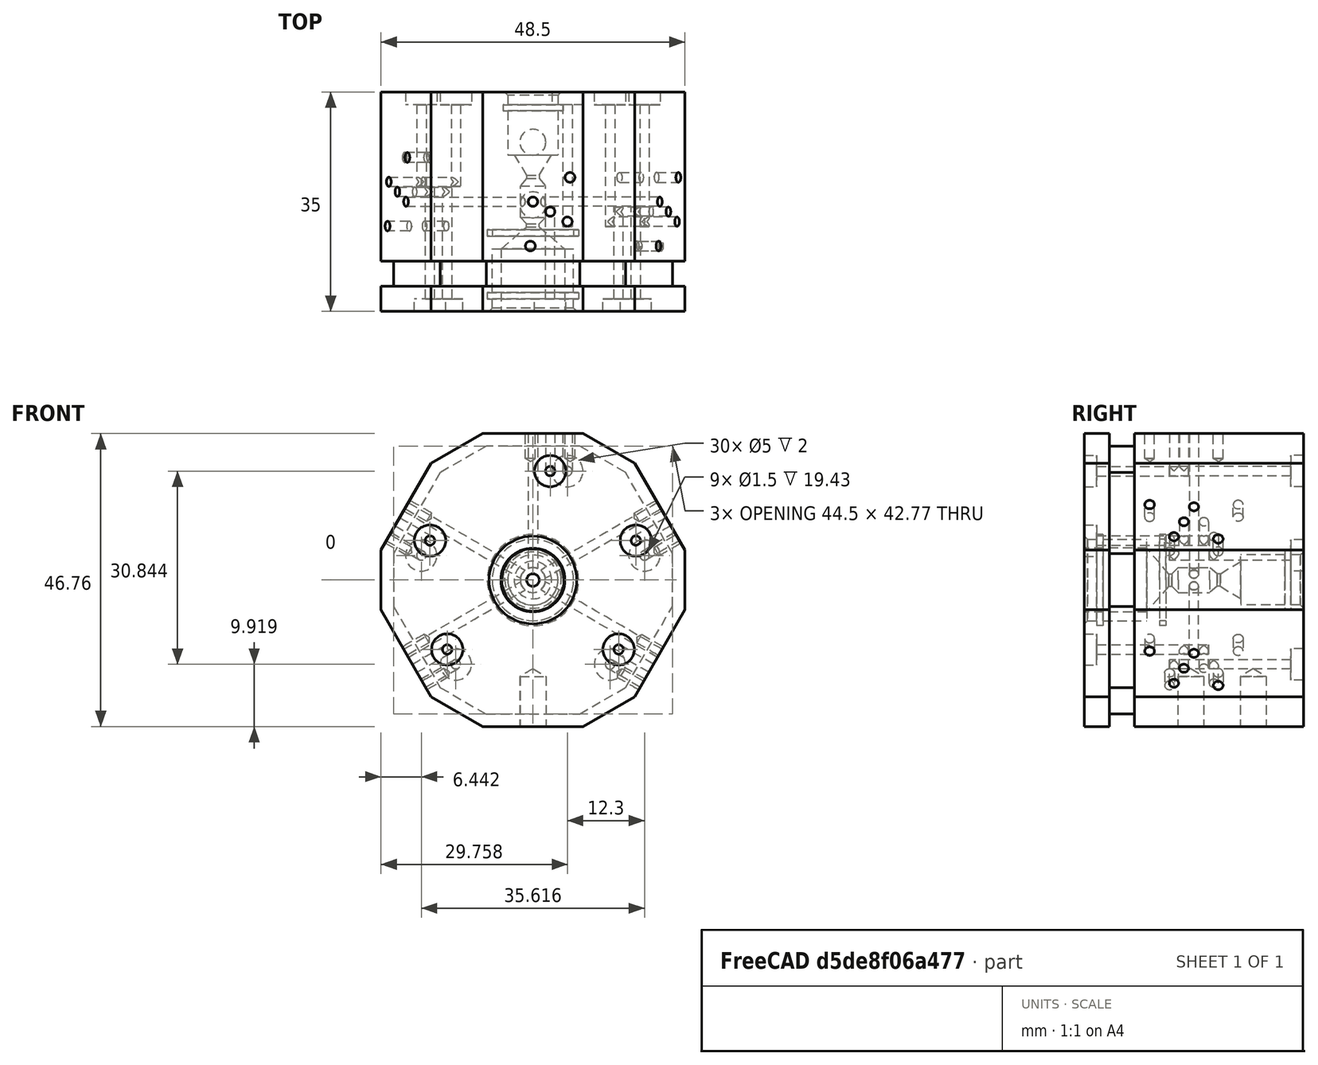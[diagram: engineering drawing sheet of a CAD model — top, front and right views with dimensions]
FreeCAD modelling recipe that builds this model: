
FCSTD DOCUMENT  (FreeCAD 0.18R16146 (Git))
Label: main
Comment: # 2020-08-05 14:49:47: read from <userpath>/repositories/sussex_neuro/Olfactometer/hardware/mechanics/from_raiser_et_al/nozzle_big.ipt
License: All rights reserved
LicenseURL: http://en.wikipedia.org/wiki/All_rights_reserved
objects: Part::Cylinder×6, Part::Feature×4, Part::MultiFuse×3, Part::Cut×3, App::FeaturePython×2, Part::Fuse×1, PartDesign::FeatureBase×1, PartDesign::Body×1
note: 19 computed .brp shape members not serialized (recipe doc carries the construction recipe); baked Part::Feature solids carry a one-line shape summary decoded from their .brp

FEATURE [Part::Feature] Part__Feature  label="main"
  shape: bbox 48.5 x 35 x 46.77 mm, 148 faces, 0 solids (baked)
FEATURE [Part::Feature] Part__Feature002  label="nozzle_small"
  Placement = pos=(0,2.5,0) rot=(-1,0,0;1.5708rad)
  shape: bbox 8 x 5 x 8 mm, 6 faces (baked)
FEATURE [Part::Feature] Part__Feature004  label="nozzle_big"
  Placement = pos=(0,-2.5,0) rot=(1,0,0;1.5708rad)
  shape: bbox 13 x 5 x 13 mm, 6 faces (baked)
FEATURE [Part::Feature] Part__Feature_solid  label="main (Solid)"
  shape: bbox 48.5 x 35 x 46.77 mm, 148 faces (baked)
FEATURE [Part::MultiFuse] Fusion  label="boddy_fusion_nozzles"
  Shapes = -> [Part__Feature002,Part__Feature004,Part__Feature_solid]
FEATURE [Part::Cylinder] Cylinder
  Angle = 360
  AttacherType = Attacher::AttachEngine3D
  Height = 4
  Placement = pos=(0,2,0) rot=(-1,0,0;1.5708rad)
  Radius = 5
FEATURE [Part::Cylinder] Cylinder001
  Angle = 360
  AttacherType = Attacher::AttachEngine3D
  Height = 11
  Placement = pos=(0,0,0) rot=(-1,0,0;1.5708rad)
  Radius = 4
FEATURE [Part::Fuse] Fusion001
  Base = -> Fusion
FEATURE [Part::Cylinder] Cylinder002
  Angle = 360
  AttacherType = Attacher::AttachEngine3D
  Height = 3
  Placement = pos=(0,-3,0) rot=(1,0,0;1.5708rad)
  Radius = 8
FEATURE [Part::Cylinder] Cylinder003
  Angle = 360
  AttacherType = Attacher::AttachEngine3D
  Height = 11
  Placement = pos=(0,0,0) rot=(1,0,0;1.5708rad)
  Radius = 6
FEATURE [Part::Cut] Cut
  Base = -> Cylinder
  Tool = -> Cylinder001
FEATURE [Part::Cut] Cut001
  Base = -> Cylinder002
  Tool = -> Cylinder003
FEATURE [Part::MultiFuse] Fusion002  label="join_cylinders_to_remove_gap"
  Shapes = -> [Fusion,Cut,Cut001]
FEATURE [PartDesign::FeatureBase] BaseFeature
  BaseFeature = -> Fusion002
FEATURE [PartDesign::Body] Body
  BaseFeature = -> Fusion002
  Group = -> [BaseFeature]
  Origin = -> Origin
  Tip = -> BaseFeature
FEATURE [App::FeaturePython] Dimension  # Draft dimension (typed FeaturePython)
  Diameter = false
  Dimline = (20.9801,-17.5,-0.0116531)
  Direction = (0,0,0)
  Distance = 13.9854
  End = (6.99466,-17.5,-0.0439505)
  Normal = (0,0,-1)
  Start = (-6.99074,-17.5,-0.076248)
FEATURE [App::FeaturePython] Dimension001  # Draft dimension (typed FeaturePython)
  Diameter = false
  Dimline = (19.4569,-16.5402,0.3547)
  Direction = (0,0,0)
  Distance = 12.9618
  End = (6.5,-16.5384,-1e-15)
  Normal = (0,0,1)
  Start = (-6.45693,-16.5366,-0.354704)
FEATURE [Part::Cylinder] Cylinder004
  Angle = 360
  AttacherType = Attacher::AttachEngine3D
  Height = 10
  Placement = pos=(0,0,0) rot=(1,0,0;1.5708rad)
  Radius = 8
FEATURE [Part::Cylinder] Cylinder005
  Angle = 360
  AttacherType = Attacher::AttachEngine3D
  Height = 12
  Placement = pos=(0,1,0) rot=(1,0,0;1.5708rad)
  Radius = 5.1
FEATURE [Part::Cut] Cut002
  Base = -> Cylinder004
  Placement = pos=(0,-7.5,0) rot=(0,0,1;0rad)
  Tool = -> Cylinder005
FEATURE [Part::MultiFuse] Fusion003  label="join_cylinder_to_fit_glass_tube"
  Shapes = -> [Cut002,Fusion002]
